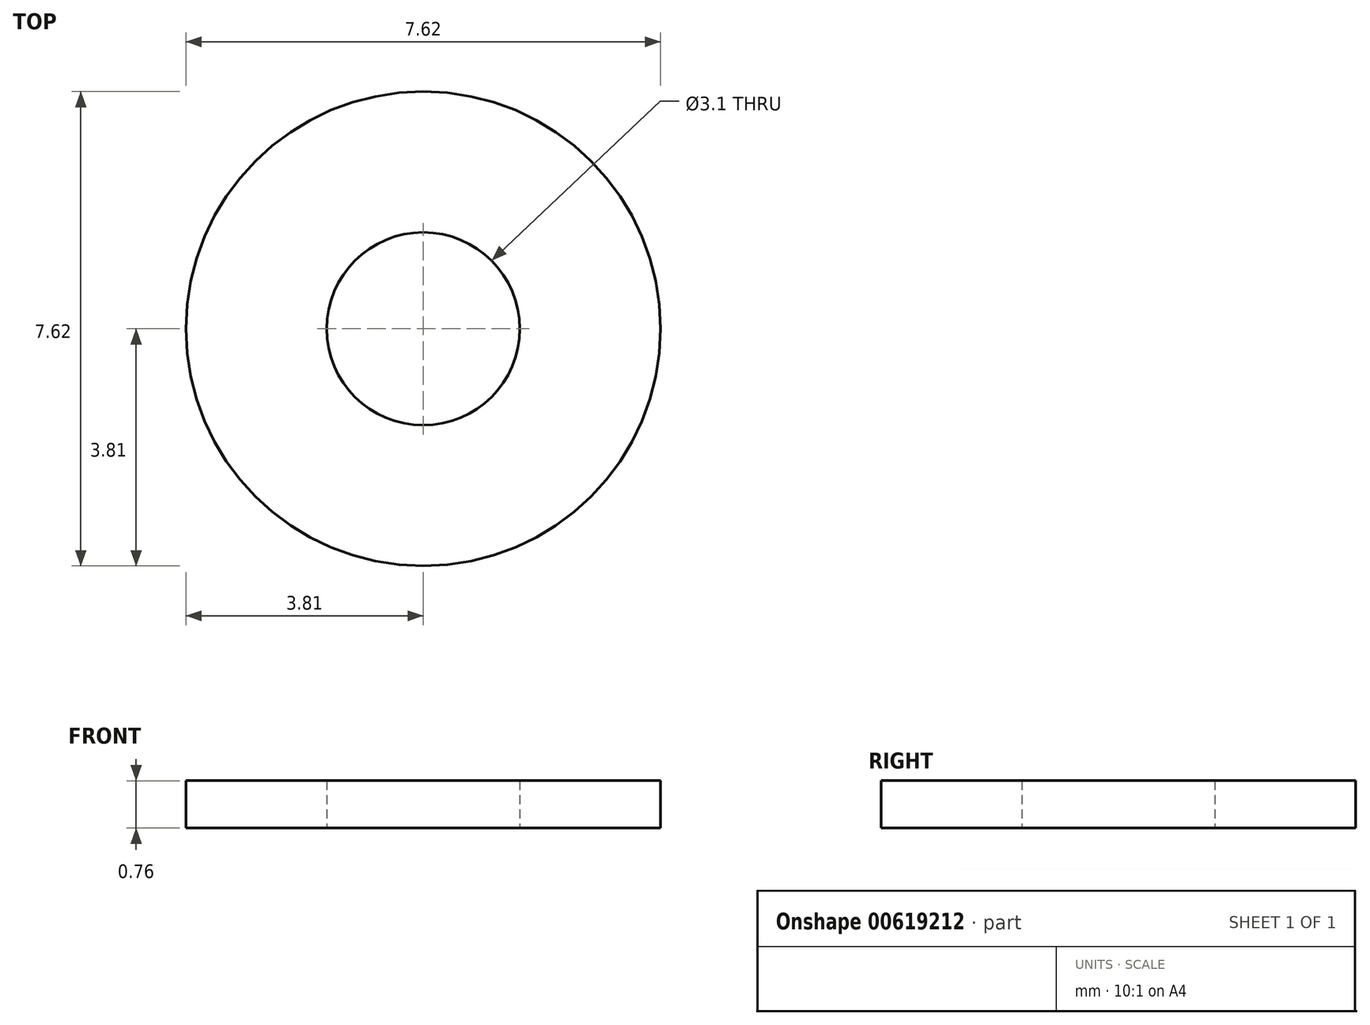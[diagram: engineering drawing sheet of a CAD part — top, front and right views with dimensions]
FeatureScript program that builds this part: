
annotation { "Feature Type Name" : "Feature", "Feature Type Description" : "" }
export const myFeature = defineFeature(function(context is Context, id is Id, definition is map)
    precondition{}
    {
        {
            var Q0;
            Q0=qCreatedBy(makeId("Top.planeOp"),FACE);
            var sketch = newSketch(context, id + "F0", { "sketchPlane" : qUnion([Q0])});
            skCircle(sketch, "E0", {"center": v(0, 0) * mm, "radius": 1.55 * mm});
            skCircle(sketch, "E1", {"center": v(0, 0) * mm, "radius": 3.81 * mm});
            skSolve(sketch);
        }
        {
            var Q0;
            Q0=makeQuery(id+"F0.imprint","IMPRINT",FACE,{"disambiguationData":[TD([[makeQuery(id+"F0.imprint","IMPRINT",EDGE,{"derivedFrom":sQuery(id+"F0.wireOp",EDGE,"E0")}),-1.0]])]});
            extrude(context, id + "F1", {"entities" : qUnion([Q0]), "depth" : 0.76 * mm, "offsetDistance" : 25.4 * mm});
        }
    });
